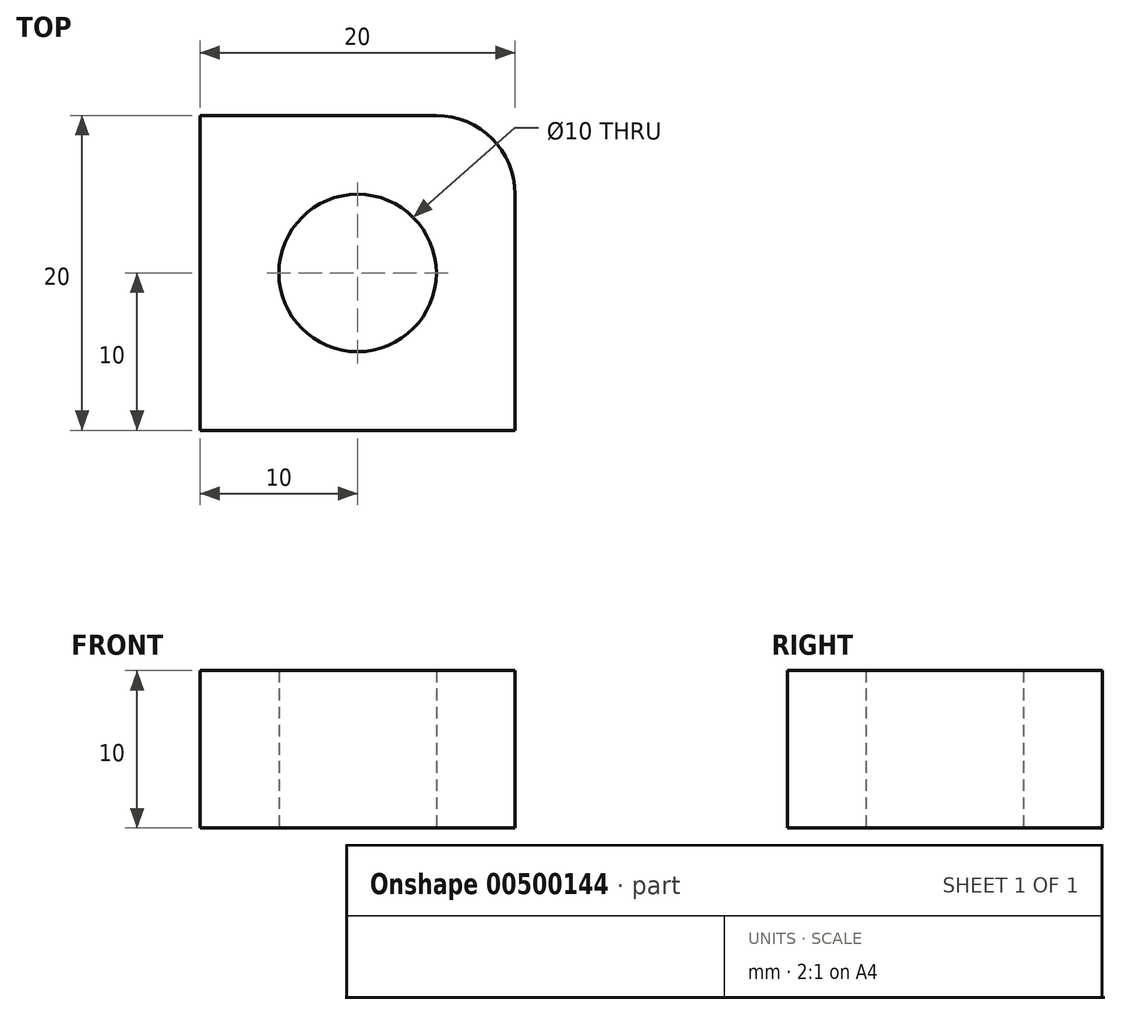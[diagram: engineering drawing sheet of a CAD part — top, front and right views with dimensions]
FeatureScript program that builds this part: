
annotation { "Feature Type Name" : "Feature", "Feature Type Description" : "" }
export const myFeature = defineFeature(function(context is Context, id is Id, definition is map)
    precondition{}
    {
        {
            var Q0;
            Q0=qCreatedBy(makeId("Top.planeOp"),FACE);
            var sketch = newSketch(context, id + "F0", { "sketchPlane" : qUnion([Q0])});
            skLineSegment(sketch, "E0.bottom", {"start": v(0, 0) * mm, "end": v(20, 0) * mm});
            skLineSegment(sketch, "E0.top", {"start": v(0, 20) * mm, "end": v(15, 20) * mm});
            skLineSegment(sketch, "E0.left", {"start": v(0, 0) * mm, "end": v(0, 20) * mm});
            skLineSegment(sketch, "E0.right", {"start": v(20, 0) * mm, "end": v(20, 15) * mm});
            skPoint(sketch, "E1.visualSharp", {"position": v(20, 20) * mm});
            skArc(sketch, "E1.filletArc", {"start": v(20, 15) * mm, "mid": v(18.54, 18.54) * mm, "end": v(15, 20) * mm});
            skCircle(sketch, "E2", {"center": v(10, 10) * mm, "radius": 5 * mm});
            skSolve(sketch);
        }
        {
            var Q0;
            Q0 = qSketchRegion(id + "F0", true);
            extrude(context, id + "F1", {"entities" : qUnion([Q0]), "depth" : 10 * mm});
        }
    });
